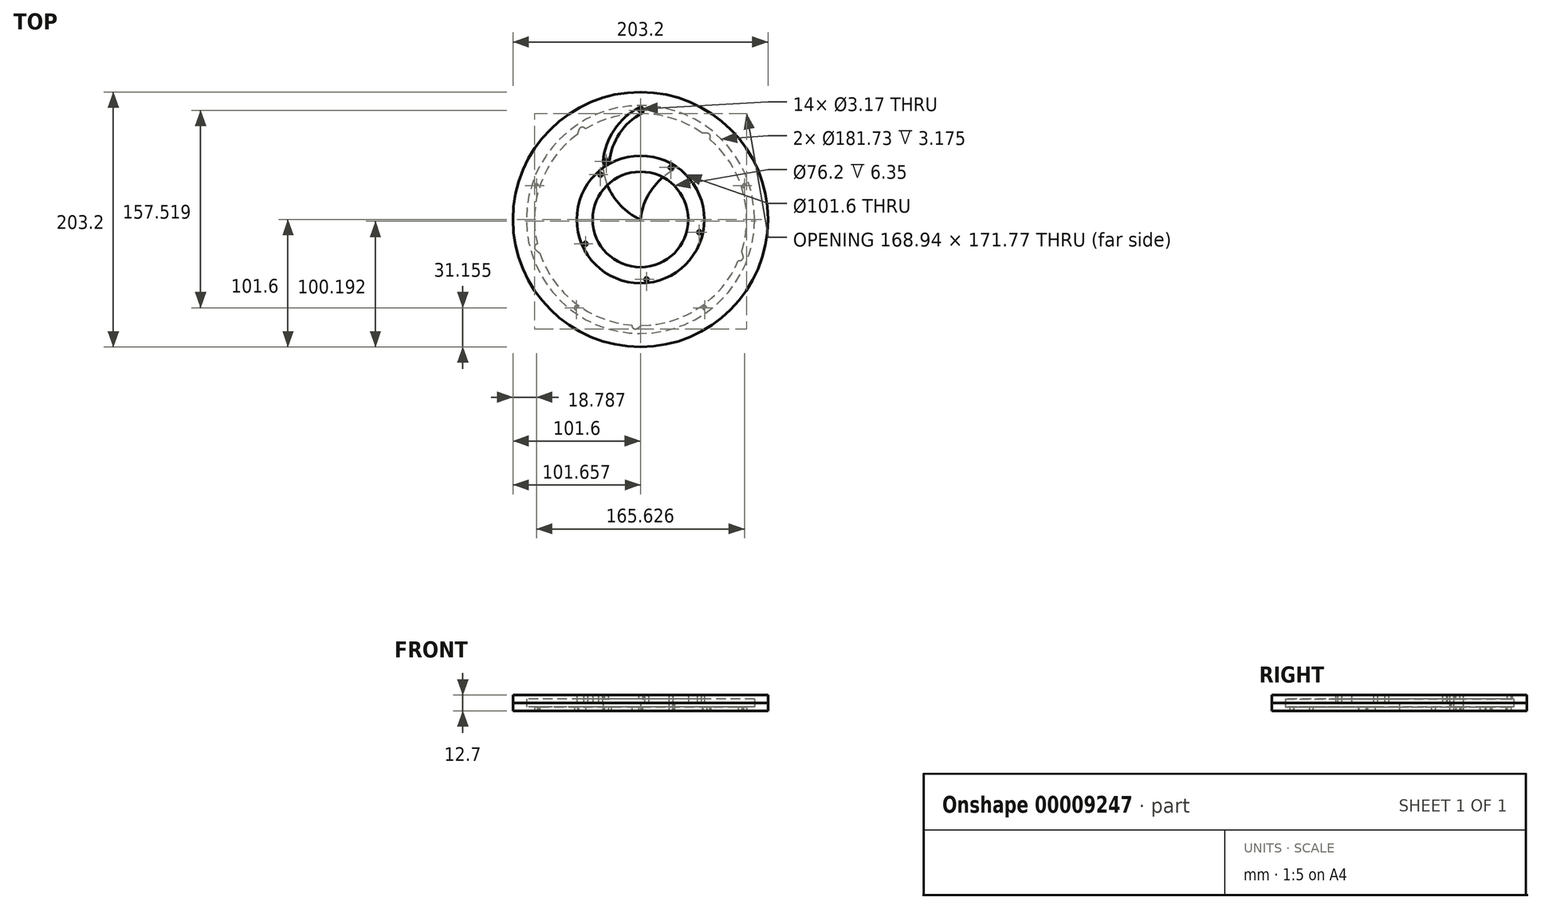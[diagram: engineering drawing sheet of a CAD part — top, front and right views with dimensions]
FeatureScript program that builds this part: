
annotation { "Feature Type Name" : "Feature", "Feature Type Description" : "" }
export const myFeature = defineFeature(function(context is Context, id is Id, definition is map)
    precondition{}
    {
        {
            var Q0;
            Q0=qCreatedBy(makeId("Top.planeOp"),FACE);
            var sketch = newSketch(context, id + "F0", { "sketchPlane" : qUnion([Q0])});
            skLineSegment(sketch, "E0", {"start": v(0, 0) * mm, "end": v(-29.86, 41.1) * mm});
            skLineSegment(sketch, "E1", {"start": v(29.86, 41.1) * mm, "end": v(0, 0) * mm});
            skArc(sketch, "E2", {"start": v(25.59, 43.89) * mm, "mid": v(-2.55, 50.74) * mm, "end": v(-29.86, 41.1) * mm});
            skCircle(sketch, "E3", {"center": v(24.15, 41.42) * mm, "radius": 1.59 * mm});
            skLineSegment(sketch, "E4", {"start": v(-29.86, 41.1) * mm, "end": v(26.99, 41.1) * mm});
            skCircle(sketch, "E5", {"center": v(-27.28, 46.2) * mm, "radius": 1.59 * mm});
            skLineSegment(sketch, "E6", {"start": v(0, 0) * mm, "end": v(0, 50.8) * mm});
            skArc(sketch, "E7", {"start": v(-29.86, 41.1) * mm, "mid": v(-20.44, 16.55) * mm, "end": v(0, 0) * mm});
            skArc(sketch, "E8", {"start": v(25.55, 38.93) * mm, "mid": v(8.05, 22.56) * mm, "end": v(0, 0) * mm});
            skArc(sketch, "E9.0", {"start": v(25.55, 38.93) * mm, "mid": v(27, 41.4) * mm, "end": v(25.59, 43.89) * mm});
            skArc(sketch, "E10.0", {"start": v(-24.75, 47.53) * mm, "mid": v(-27.97, 48.98) * mm, "end": v(-30.14, 46.2) * mm});
            skArc(sketch, "E11", {"start": v(-30.14, 46.2) * mm, "mid": v(-30.06, 43.64) * mm, "end": v(-29.86, 41.1) * mm});
            skLineSegment(sketch, "E12", {"start": v(-24.75, 47.53) * mm, "end": v(-23.46, 45.06) * mm});
            skSolve(sketch);
        }
        {
            var Q0;
            Q0=makeQuery(id+"F0.imprint","IMPRINT",FACE,{"disambiguationData":[TD([[makeQuery(id+"F0.imprint","IMPRINT",EDGE,{"derivedFrom":sQuery(id+"F0.wireOp",EDGE,"E1")}),1.0]])]});
            var Q1;
            {var subQ4=sQuery(id+"F0.wireOp",EDGE,"cdf5fea3-dff5-4225-ba3e-658a99759021");Q1=makeQuery(id+"F0.imprint","IMPRINT",FACE,{"disambiguationData":[TD([[makeQuery(id+"F0.imprint","IMPRINT",EDGE,{"derivedFrom":subQ4}),-1.0]])]});}
            var Q2;
            {var subQ3=sQuery(id+"F0.wireOp",EDGE,"E0");Q2=makeQuery(id+"F0.imprint","IMPRINT",FACE,{"disambiguationData":[TD([[makeQuery(id+"F0.imprint","IMPRINT",EDGE,{"derivedFrom":subQ3}),-1.0]])]});}
            var Q3;
            Q3=makeQuery(id+"F0.imprint","IMPRINT",FACE,{"disambiguationData":[TD([[makeQuery(id+"F0.imprint","IMPRINT",EDGE,{"derivedFrom":sQuery(id+"F0.wireOp",EDGE,"E0")}),1.0]])]});
            var Q4;
            {var subQ3=sQuery(id+"F0.wireOp",EDGE,"E4");var subQ5=sQuery(id+"F0.wireOp",EDGE,"E6");var subQ7=makeQuery(id+"F0.imprint","INTERSECT",VERTEX,{"derivedFrom":[subQ3,subQ5]});Q4=makeQuery(id+"F0.imprint","IMPRINT",FACE,{"disambiguationData":[TD([[makeQuery(id+"F0.imprint","IMPRINT",EDGE,{"disambiguationData":[TD([[subQ7,-1.0]])],"derivedFrom":subQ3}),-1.0]])]});}
            var Q5;
            {var subQ3=sQuery(id+"F0.wireOp",EDGE,"E2");var subQ5=sQuery(id+"F0.wireOp",EDGE,"E6");var subQ7=makeQuery(id+"F0.imprint","INTERSECT",VERTEX,{"derivedFrom":[subQ3,subQ5]});Q5=makeQuery(id+"F0.imprint","IMPRINT",FACE,{"disambiguationData":[TD([[makeQuery(id+"F0.imprint","IMPRINT",EDGE,{"disambiguationData":[TD([[subQ7,1.0]])],"derivedFrom":subQ3}),1.0]])]});}
            var Q6;
            {var subQ1=sQuery(id+"F0.wireOp",EDGE,"E4");var subQ5=sQuery(id+"F0.wireOp",EDGE,"E5");var subQ6=makeQuery(id+"F0.imprint","INTERSECT",VERTEX,{"disambiguationData":[OD(1.0)],"derivedFrom":[subQ1,subQ5]});Q6=makeQuery(id+"F0.imprint","IMPRINT",FACE,{"disambiguationData":[TD([[makeQuery(id+"F0.imprint","IMPRINT",EDGE,{"disambiguationData":[TD([[subQ6,-1.0]])],"derivedFrom":subQ1}),1.0]])]});}
            var Q7;
            {var subQ2=sQuery(id+"F0.wireOp",EDGE,"E4");var subQ5=sQuery(id+"F0.wireOp",EDGE,"E3");var subQ7=makeQuery(id+"F0.imprint","INTERSECT",VERTEX,{"disambiguationData":[OD(0.0)],"derivedFrom":[subQ5,subQ2]});Q7=makeQuery(id+"F0.imprint","IMPRINT",FACE,{"disambiguationData":[TD([[makeQuery(id+"F0.imprint","IMPRINT",EDGE,{"disambiguationData":[TD([[subQ7,-1.0]])],"derivedFrom":subQ5}),-1.0]])]});}
            var Q8;
            {var subQ1=sQuery(id+"F0.wireOp",EDGE,"E4");var subQ5=sQuery(id+"F0.wireOp",EDGE,"E3");var subQ7=makeQuery(id+"F0.imprint","INTERSECT",VERTEX,{"disambiguationData":[OD(0.0)],"derivedFrom":[subQ5,subQ1]});Q8=makeQuery(id+"F0.imprint","IMPRINT",FACE,{"disambiguationData":[TD([[makeQuery(id+"F0.imprint","IMPRINT",EDGE,{"disambiguationData":[TD([[subQ7,1.0]])],"derivedFrom":subQ5}),-1.0]])]});}
            var Q9;
            {var subQ0=sQuery(id+"F0.wireOp",EDGE,"E10.0");var subQ1=sQuery(id+"F0.wireOp",EDGE,"E4");var subQ2=makeQuery(id+"F0.imprint","INTERSECT",VERTEX,{"disambiguationData":[OD(1.0)],"derivedFrom":[subQ1,subQ0]});Q9=makeQuery(id+"F0.imprint","IMPRINT",FACE,{"disambiguationData":[TD([[makeQuery(id+"F0.imprint","IMPRINT",EDGE,{"disambiguationData":[TD([[subQ2,-1.0]])],"derivedFrom":subQ1}),-1.0]])]});}
            var Q10;
            {var subQ3=sQuery(id+"F0.wireOp",EDGE,"E2");var subQ5=sQuery(id+"F0.wireOp",EDGE,"E6");var subQ7=makeQuery(id+"F0.imprint","INTERSECT",VERTEX,{"derivedFrom":[subQ3,subQ5]});Q10=makeQuery(id+"F0.imprint","IMPRINT",FACE,{"disambiguationData":[TD([[makeQuery(id+"F0.imprint","IMPRINT",EDGE,{"disambiguationData":[TD([[subQ7,-1.0]])],"derivedFrom":subQ3}),1.0]])]});}
            var Q11;
            {var subQ0=sQuery(id+"F0.wireOp",EDGE,"E10.0");var subQ3=sQuery(id+"F0.wireOp",EDGE,"E2");var subQ4=makeQuery(id+"F0.imprint","INTERSECT",VERTEX,{"derivedFrom":[subQ3,subQ0]});Q11=makeQuery(id+"F0.imprint","IMPRINT",FACE,{"disambiguationData":[TD([[makeQuery(id+"F0.imprint","IMPRINT",EDGE,{"disambiguationData":[TD([[subQ4,-1.0]])],"derivedFrom":subQ0}),-1.0]])]});}
            extrude(context, id + "F1", {"entities" : qUnion([Q0, Q1, Q2, Q3, Q4, Q5, Q6, Q7, Q8, Q9, Q10, Q11]), "depth" : 6.35 * mm});
        }
        {
            var Q0;
            Q0=makeQuery(id+"F0.imprint","IMPRINT",FACE,{"disambiguationData":[TD([[makeQuery(id+"F0.imprint","IMPRINT",EDGE,{"derivedFrom":sQuery(id+"F0.wireOp",EDGE,"E5")}),-1.0]])]});
            extrude(context, id + "F2", {"entities" : qUnion([Q0]), "operationType" : NewBodyOperationType.ADD, "depth" : 3.17 * mm});
        }
        {
            var Q0;
            Q0=makeQuery(id+"F1.opExtrude","CAP_FACE",FACE,{"disambiguationData":[OSD([sQuery(id+"F0.wireOp",EDGE,"E2"),sQuery(id+"F0.wireOp",EDGE,"E3"),sQuery(id+"F0.wireOp",EDGE,"E5"),sQuery(id+"F0.wireOp",EDGE,"E7"),sQuery(id+"F0.wireOp",EDGE,"E8")])],"isStart":false});
            var sketch = newSketch(context, id + "F3", { "sketchPlane" : qUnion([Q0])});
            skArc(sketch, "E13", {"start": v(-29.8, 46.44) * mm, "mid": v(-27.52, 43.68) * mm, "end": v(-24.75, 45.97) * mm});
            skArc(sketch, "E14", {"start": v(1.19, 84.83) * mm, "mid": v(-16.7, 68.68) * mm, "end": v(-24.75, 45.97) * mm});
            skArc(sketch, "E15", {"start": v(1.19, 84.83) * mm, "mid": v(2.25, 88.26) * mm, "end": v(-1.19, 89.32) * mm});
            skArc(sketch, "E16", {"start": v(-1.19, 89.32) * mm, "mid": v(-20.92, 71.5) * mm, "end": v(-29.8, 46.44) * mm});
            skCircle(sketch, "E17", {"center": v(-27.28, 46.2) * mm, "radius": 1.59 * mm});
            skCircle(sketch, "E18", {"center": v(0, 87.07) * mm, "radius": 1.59 * mm});
            skLineSegment(sketch, "E19", {"start": v(-29.45, 49.42) * mm, "end": v(-24.42, 48.67) * mm});
            skSolve(sketch);
        }
        {
            var Q0;
            {var subQ5=sQuery(id+"F3.wireOp",EDGE,"E15");Q0=makeQuery(id+"F3.imprint","IMPRINT",FACE,{"disambiguationData":[TD([[makeQuery(id+"F3.imprint","IMPRINT",EDGE,{"derivedFrom":subQ5}),1.0]])]});}
            var Q1;
            {var subQ5=sQuery(id+"F3.wireOp",EDGE,"E13");Q1=makeQuery(id+"F3.imprint","IMPRINT",FACE,{"disambiguationData":[TD([[makeQuery(id+"F3.imprint","IMPRINT",EDGE,{"derivedFrom":subQ5}),1.0]])]});}
            var Q2;
            {var subQ1=sQuery(id+"F3.wireOp",EDGE,"E14");var subQ5=sQuery(id+"F3.wireOp",EDGE,"25e74c22-3269-4606-a573-f221d8978cd7");var subQ7=makeQuery(id+"F3.imprint","INTERSECT",VERTEX,{"disambiguationData":[OD(1.0)],"derivedFrom":[subQ1,subQ5]});Q2=makeQuery(id+"F3.imprint","IMPRINT",FACE,{"disambiguationData":[TD([[makeQuery(id+"F3.imprint","IMPRINT",EDGE,{"disambiguationData":[TD([[subQ7,-1.0]])],"derivedFrom":subQ1}),-1.0]])]});}
            var Q3;
            {var subQ1=sQuery(id+"F3.wireOp",EDGE,"E19");var subQ3=sQuery(id+"F3.wireOp",EDGE,"E16");var subQ5=makeQuery(id+"F3.imprint","INTERSECT",VERTEX,{"derivedFrom":[subQ3,subQ1]});Q3=makeQuery(id+"F3.imprint","IMPRINT",FACE,{"disambiguationData":[TD([[makeQuery(id+"F3.imprint","IMPRINT",EDGE,{"disambiguationData":[TD([[subQ5,-1.0]])],"derivedFrom":subQ3}),1.0]])]});}
            var Q4;
            {var subQ1=sQuery(id+"F3.wireOp",EDGE,"E14");var subQ7=sQuery(id+"F3.wireOp",EDGE,"E19");var subQ9=makeQuery(id+"F3.imprint","INTERSECT",VERTEX,{"derivedFrom":[subQ1,subQ7]});Q4=makeQuery(id+"F3.imprint","IMPRINT",FACE,{"disambiguationData":[TD([[makeQuery(id+"F3.imprint","IMPRINT",EDGE,{"disambiguationData":[TD([[subQ9,-1.0]])],"derivedFrom":subQ1}),-1.0]])]});}
            var Q5;
            {var subQ1=sQuery(id+"F3.wireOp",EDGE,"E19");var subQ3=sQuery(id+"F3.wireOp",EDGE,"25e74c22-3269-4606-a573-f221d8978cd7");var subQ5=makeQuery(id+"F3.imprint","INTERSECT",VERTEX,{"derivedFrom":[subQ3,subQ1]});Q5=makeQuery(id+"F3.imprint","IMPRINT",FACE,{"disambiguationData":[TD([[makeQuery(id+"F3.imprint","IMPRINT",EDGE,{"disambiguationData":[TD([[subQ5,-1.0]])],"derivedFrom":subQ3}),-1.0]])]});}
            extrude(context, id + "F4", {"entities" : qUnion([Q0, Q1, Q2, Q3, Q4, Q5]), "depth" : 6.35 * mm});
        }
        {
            var Q0;
            Q0=qCreatedBy(makeId("Top.planeOp"),FACE);
            var sketch = newSketch(context, id + "F5", { "sketchPlane" : qUnion([Q0])});
            skArc(sketch, "E20", {"start": v(-50.23, 68) * mm, "mid": v(-79.38, 29.08) * mm, "end": v(-82.27, -19.46) * mm});
            skCircle(sketch, "E21.0", {"center": v(0, 0) * mm, "radius": 101.6 * mm});
            skCircle(sketch, "E22", {"center": v(0, 87.07) * mm, "radius": 1.59 * mm});
            skCircle(sketch, "E23.1.0", {"center": v(-82.81, 26.9) * mm, "radius": 1.59 * mm});
            skCircle(sketch, "E23.2.0", {"center": v(-51.18, -70.44) * mm, "radius": 1.59 * mm});
            skCircle(sketch, "E23.3.0", {"center": v(51.18, -70.44) * mm, "radius": 1.59 * mm});
            skCircle(sketch, "E23.4.0", {"center": v(82.81, 26.9) * mm, "radius": 1.59 * mm});
            skArc(sketch, "E24", {"start": v(-49.02, 71.7) * mm, "mid": v(-49.66, 69.85) * mm, "end": v(-50.23, 68) * mm});
            skArc(sketch, "E25", {"start": v(2.35, 49.95) * mm, "mid": v(-21.6, 66.25) * mm, "end": v(-50.55, 66.83) * mm});
            skArc(sketch, "E26.converted", {"start": v(-43.93, 72.23) * mm, "mid": v(-46.64, 73.54) * mm, "end": v(-49.02, 71.7) * mm});
            skLineSegment(sketch, "E27", {"start": v(2.35, 49.95) * mm, "end": v(-0.11, 47.94) * mm});
            skArc(sketch, "E28.0", {"start": v(24.2, 41.38) * mm, "mid": v(0.38, 47.94) * mm, "end": v(-23.54, 41.76) * mm});
            skArc(sketch, "E29.1.0", {"start": v(-82.27, -19.46) * mm, "mid": v(-84.36, -21.63) * mm, "end": v(-83.33, -24.47) * mm});
            skArc(sketch, "E29.1.1", {"start": v(-83.33, -24.47) * mm, "mid": v(-81.78, -25.65) * mm, "end": v(-80.19, -26.76) * mm});
            skArc(sketch, "E29.2.0", {"start": v(-6.92, -84.25) * mm, "mid": v(-5.5, -86.91) * mm, "end": v(-2.48, -86.81) * mm});
            skArc(sketch, "E29.2.1", {"start": v(-2.48, -86.81) * mm, "mid": v(-0.88, -85.7) * mm, "end": v(0.68, -84.53) * mm});
            skArc(sketch, "E29.3.0", {"start": v(77.99, -32.61) * mm, "mid": v(80.96, -32.08) * mm, "end": v(81.8, -29.19) * mm});
            skArc(sketch, "E29.3.1", {"start": v(81.8, -29.19) * mm, "mid": v(81.24, -27.32) * mm, "end": v(80.6, -25.48) * mm});
            skArc(sketch, "E29.4.0", {"start": v(55.12, 64.1) * mm, "mid": v(55.53, 67.08) * mm, "end": v(53.04, 68.78) * mm});
            skArc(sketch, "E29.4.1", {"start": v(53.04, 68.78) * mm, "mid": v(51.09, 68.82) * mm, "end": v(49.14, 68.78) * mm});
            skCircle(sketch, "E30", {"center": v(0, 0) * mm, "radius": 90.86 * mm});
            skLineSegment(sketch, "E31", {"start": v(-46.34, 70.7) * mm, "end": v(0, 87.07) * mm});
            skCircle(sketch, "E32", {"center": v(0, 0) * mm, "radius": 38.1 * mm});
            skPoint(sketch, "E33.orphan", {"position": v(47.93, 68.73) * mm});
            skArc(sketch, "E34.trimOffspring", {"start": v(49.14, 68.78) * mm, "mid": v(3.12, 84.48) * mm, "end": v(-43.93, 72.23) * mm});
            skPoint(sketch, "E35.orphan", {"position": v(80.18, -24.35) * mm});
            skArc(sketch, "E36.trimOffspring", {"start": v(80.6, -25.48) * mm, "mid": v(81.3, 23.13) * mm, "end": v(55.12, 64.1) * mm});
            skArc(sketch, "E37.trimOffspring", {"start": v(0.68, -84.53) * mm, "mid": v(47.13, -70.18) * mm, "end": v(77.99, -32.61) * mm});
            skPoint(sketch, "E38.orphan", {"position": v(1.62, -83.78) * mm});
            skArc(sketch, "E39.trimOffspring", {"start": v(-80.19, -26.76) * mm, "mid": v(-52.18, -66.5) * mm, "end": v(-6.92, -84.25) * mm});
            skPoint(sketch, "E40.orphan", {"position": v(-79.18, -27.43) * mm});
            skSolve(sketch);
        }
        {
            var Q0;
            Q0=makeQuery(id+"F5.imprint","IMPRINT",FACE,{"disambiguationData":[TD([[makeQuery(id+"F5.imprint","IMPRINT",EDGE,{"derivedFrom":sQuery(id+"F5.wireOp",EDGE,"E22")}),-1.0]])]});
            extrude(context, id + "F6", {"entities" : qUnion([Q0]), "depth" : 3.17 * mm});
        }
        {
            var Q0;
            Q0=makeQuery(id+"F5.imprint","IMPRINT",FACE,{"disambiguationData":[TD([[makeQuery(id+"F5.imprint","IMPRINT",EDGE,{"derivedFrom":sQuery(id+"F5.wireOp",EDGE,"E21.0")}),1.0]])]});
            extrude(context, id + "F7", {"entities" : qUnion([Q0]), "operationType" : NewBodyOperationType.ADD, "depth" : 6.35 * mm});
        }
        {
            var Q0;
            Q0=makeQuery(id+"F1.opExtrude","CAP_FACE",FACE,{"disambiguationData":[OSD([sQuery(id+"F0.wireOp",EDGE,"E2"),sQuery(id+"F0.wireOp",EDGE,"cdf5fea3-dff5-4225-ba3e-658a99759021"),sQuery(id+"F0.wireOp",EDGE,"c6d38945-63b1-47df-b09c-852a8a832c86")])],"isStart":false});
            var sketch = newSketch(context, id + "F8", { "sketchPlane" : qUnion([Q0])});
            skCircle(sketch, "E41", {"center": v(0, 0) * mm, "radius": 38.1 * mm});
            skCircle(sketch, "E42", {"center": v(24.15, 41.42) * mm, "radius": 1.59 * mm});
            skCircle(sketch, "E43.1.0", {"center": v(-31.93, 35.76) * mm, "radius": 1.59 * mm});
            skCircle(sketch, "E43.2.0", {"center": v(-43.88, -19.31) * mm, "radius": 1.59 * mm});
            skCircle(sketch, "E43.3.0", {"center": v(4.8, -47.7) * mm, "radius": 1.59 * mm});
            skCircle(sketch, "E43.4.0", {"center": v(46.85, -10.17) * mm, "radius": 1.59 * mm});
            skCircle(sketch, "E44.0", {"center": v(0, 0) * mm, "radius": 50.8 * mm});
            skSolve(sketch);
        }
        {
            var Q0;
            Q0 = qSketchRegion(id + "F8", true);
            extrude(context, id + "F9", {"entities" : qUnion([Q0]), "depth" : 6.35 * mm});
        }
        {
            var Q0;
            Q0=makeQuery(id+"F9.opExtrude","CAP_FACE",FACE,{"disambiguationData":[OSD([sQuery(id+"F8.wireOp",EDGE,"89fc57cc-10c5-4f8b-a67a-50b32ee3bc6c"),sQuery(id+"F8.wireOp",EDGE,"E41"),sQuery(id+"F8.wireOp",EDGE,"E42"),sQuery(id+"F8.wireOp",EDGE,"E43.1.0"),sQuery(id+"F8.wireOp",EDGE,"E43.2.0"),sQuery(id+"F8.wireOp",EDGE,"E43.3.0"),sQuery(id+"F8.wireOp",EDGE,"E43.4.0"),sQuery(id+"F8.wireOp",EDGE,"09c93f8d-0898-4539-8e24-536939b80a2e"),sQuery(id+"F8.wireOp",EDGE,"2e7c2fb3-dce8-46eb-bc5c-eceb78e0b5b5"),sQuery(id+"F8.wireOp",EDGE,"8d48d3cc-4478-427a-a2d0-19994bf38308"),sQuery(id+"F8.wireOp",EDGE,"b4ea9f8c-d97a-49db-bb95-a072d4a73806.1.0"),sQuery(id+"F8.wireOp",EDGE,"b4ea9f8c-d97a-49db-bb95-a072d4a73806.1.1"),sQuery(id+"F8.wireOp",EDGE,"b4ea9f8c-d97a-49db-bb95-a072d4a73806.1.2"),sQuery(id+"F8.wireOp",EDGE,"b4ea9f8c-d97a-49db-bb95-a072d4a73806.2.0"),sQuery(id+"F8.wireOp",EDGE,"b4ea9f8c-d97a-49db-bb95-a072d4a73806.2.1"),sQuery(id+"F8.wireOp",EDGE,"b4ea9f8c-d97a-49db-bb95-a072d4a73806.2.2"),sQuery(id+"F8.wireOp",EDGE,"b4ea9f8c-d97a-49db-bb95-a072d4a73806.3.0"),sQuery(id+"F8.wireOp",EDGE,"b4ea9f8c-d97a-49db-bb95-a072d4a73806.3.1"),sQuery(id+"F8.wireOp",EDGE,"b4ea9f8c-d97a-49db-bb95-a072d4a73806.3.2"),sQuery(id+"F8.wireOp",EDGE,"b4ea9f8c-d97a-49db-bb95-a072d4a73806.4.0"),sQuery(id+"F8.wireOp",EDGE,"b4ea9f8c-d97a-49db-bb95-a072d4a73806.4.1"),sQuery(id+"F8.wireOp",EDGE,"b4ea9f8c-d97a-49db-bb95-a072d4a73806.4.2"),sQuery(id+"F8.wireOp",EDGE,"62629d59-98e2-414c-a4a6-2e01639a4139.trimOffspring"),sQuery(id+"F8.wireOp",EDGE,"4f264073-deaa-4671-b40b-d728fd01fa4f.trimOffspring"),sQuery(id+"F8.wireOp",EDGE,"41f4ab78-ba68-4a2b-b3e8-ce39d1aeb1a1.trimOffspring"),sQuery(id+"F8.wireOp",EDGE,"7c5c2c69-9f82-4033-9fd1-45fc17a03532.trimOffspring")])],"isStart":false});
            var sketch = newSketch(context, id + "F10", { "sketchPlane" : qUnion([Q0])});
            skCircle(sketch, "E45", {"center": v(24.15, 41.42) * mm, "radius": 1.59 * mm});
            skSolve(sketch);
        }
        {
            var Q0;
            Q0 = qSketchRegion(id + "F10", true);
            extrude(context, id + "F11", {"entities" : qUnion([Q0]), "oppositeDirection" : true, "depth" : 12.7 * mm});
        }
        {
            var Q0;
            Q0=makeQuery(id+"F7.opExtrude","CAP_FACE",FACE,{"disambiguationData":[OSD([sQuery(id+"F5.wireOp",EDGE,"E21.0"),sQuery(id+"F5.wireOp",EDGE,"E30")])],"isStart":false});
            var sketch = newSketch(context, id + "F12", { "sketchPlane" : qUnion([Q0])});
            skCircle(sketch, "E46", {"center": v(0, 0) * mm, "radius": 101.6 * mm});
            skCircle(sketch, "E47", {"center": v(0, 0) * mm, "radius": 90.86 * mm});
            skCircle(sketch, "E48", {"center": v(0, 0) * mm, "radius": 50.8 * mm});
            skSolve(sketch);
        }
        {
            var Q0;
            Q0 = qSketchRegion(id + "F12", true);
            var Q1;
            Q1=makeQuery(id+"F12.imprint","IMPRINT",FACE,{"disambiguationData":[TD([[makeQuery(id+"F12.imprint","IMPRINT",EDGE,{"derivedFrom":sQuery(id+"F12.wireOp",EDGE,"E47")}),1.0]])]});
            extrude(context, id + "F13", {"entities" : qUnion([Q0, Q1]), "depth" : 6.35 * mm});
        }
        {
            var Q0;
            Q0=makeQuery(id+"F12.imprint","IMPRINT",FACE,{"disambiguationData":[TD([[makeQuery(id+"F12.imprint","IMPRINT",EDGE,{"derivedFrom":sQuery(id+"F12.wireOp",EDGE,"E47")}),1.0]])]});
            extrude(context, id + "F14", {"entities" : qUnion([Q0]), "operationType" : NewBodyOperationType.REMOVE, "depth" : 3.17 * mm});
        }
    });
